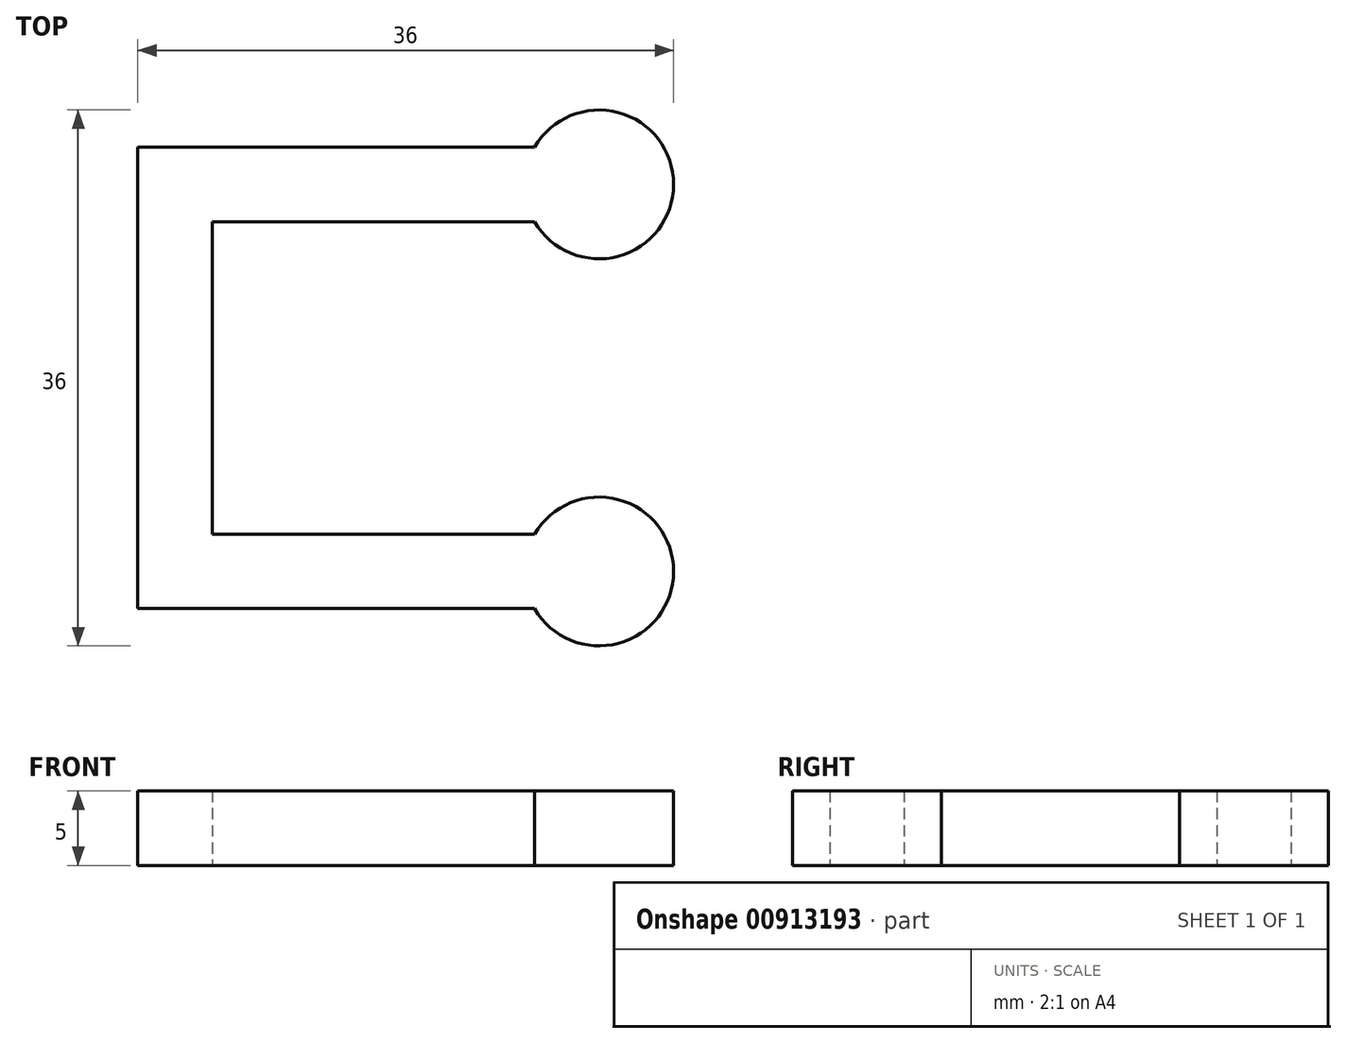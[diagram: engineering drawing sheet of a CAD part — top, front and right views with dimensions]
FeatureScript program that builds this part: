
annotation { "Feature Type Name" : "Feature", "Feature Type Description" : "" }
export const myFeature = defineFeature(function(context is Context, id is Id, definition is map)
    precondition{}
    {
        {
            assignVariable(context, id + "F0", {"name" : "HangerThickness", "anyValue" : 5});
        }
        {
            var Q0;
            Q0=qCreatedBy(makeId("Top.planeOp"),FACE);
            var sketch = newSketch(context, id + "F1", { "sketchPlane" : qUnion([Q0])});
            skLineSegment(sketch, "E0.bottom", {"start": v(10.5, 10.5) * mm, "end": v(-10.5, 10.5) * mm});
            skLineSegment(sketch, "E0.top", {"start": v(10.5, -10.5) * mm, "end": v(-10.5, -10.5) * mm});
            skLineSegment(sketch, "E0.left", {"start": v(10.5, 10.5) * mm, "end": v(10.5, -10.5) * mm});
            skLineSegment(sketch, "E0.right", {"start": v(-10.5, 10.5) * mm, "end": v(-10.5, -10.5) * mm});
            skPoint(sketch, "E0.middle", {"position": v(0, 0) * mm});
            skLineSegment(sketch, "E1.bottom", {"start": v(-15.5, 15.5) * mm, "end": v(15.5, 15.5) * mm});
            skLineSegment(sketch, "E1.top", {"start": v(-15.5, 10.5) * mm, "end": v(15.5, 10.5) * mm});
            skLineSegment(sketch, "E1.left", {"start": v(-15.5, 15.5) * mm, "end": v(-15.5, 10.5) * mm});
            skLineSegment(sketch, "E1.right", {"start": v(15.5, 15.5) * mm, "end": v(15.5, 10.5) * mm});
            skPoint(sketch, "E2", {"position": v(0, 10.5) * mm});
            skLineSegment(sketch, "E3.bottom", {"start": v(-10.5, 10.5) * mm, "end": v(-15.5, 10.5) * mm});
            skLineSegment(sketch, "E3.top", {"start": v(-10.5, -15.5) * mm, "end": v(-15.5, -15.5) * mm});
            skLineSegment(sketch, "E3.left", {"start": v(-10.5, 10.5) * mm, "end": v(-10.5, -15.5) * mm});
            skLineSegment(sketch, "E3.right", {"start": v(-15.5, 10.5) * mm, "end": v(-15.5, -15.5) * mm});
            skPoint(sketch, "E4", {"position": v(-13, -15.5) * mm});
            skPoint(sketch, "E5", {"position": v(15.5, 13) * mm});
            skCircle(sketch, "E6", {"center": v(15.5, 13) * mm, "radius": 5 * mm});
            skLineSegment(sketch, "E7.bottom", {"start": v(-10.5, -15.5) * mm, "end": v(15.5, -15.5) * mm});
            skLineSegment(sketch, "E7.top", {"start": v(-10.5, -10.5) * mm, "end": v(15.5, -10.5) * mm});
            skLineSegment(sketch, "E7.left", {"start": v(-10.5, -15.5) * mm, "end": v(-10.5, -10.5) * mm});
            skLineSegment(sketch, "E7.right", {"start": v(15.5, -15.5) * mm, "end": v(15.5, -10.5) * mm});
            skPoint(sketch, "E8", {"position": v(15.5, -13) * mm});
            skCircle(sketch, "E9", {"center": v(15.5, -13) * mm, "radius": 5 * mm});
            skSolve(sketch);
        }
        {
            var Q0;
            {var subQ0=sQuery(id+"F1.wireOp",EDGE,"E3.top");Q0=makeQuery(id+"F1.imprint","IMPRINT",FACE,{"disambiguationData":[TD([[makeQuery(id+"F1.imprint","IMPRINT",EDGE,{"derivedFrom":subQ0}),1.0]])]});}
            var Q1;
            {var subQ1=sQuery(id+"F1.wireOp",EDGE,"E0.right");Q1=makeQuery(id+"F1.imprint","IMPRINT",FACE,{"disambiguationData":[TD([[makeQuery(id+"F1.imprint","IMPRINT",EDGE,{"derivedFrom":subQ1}),-1.0]])]});}
            var Q2;
            {var subQ1=sQuery(id+"F1.wireOp",EDGE,"E0.right");Q2=makeQuery(id+"F1.imprint","IMPRINT",FACE,{"disambiguationData":[TD([[makeQuery(id+"F1.imprint","IMPRINT",EDGE,{"derivedFrom":subQ1}),-1.0]])]});}
            var Q3;
            {var subQ1=sQuery(id+"F1.wireOp",EDGE,"E0.bottom");Q3=makeQuery(id+"F1.imprint","IMPRINT",FACE,{"disambiguationData":[TD([[makeQuery(id+"F1.imprint","IMPRINT",EDGE,{"derivedFrom":subQ1}),-1.0]])]});}
            var Q4;
            {var subQ0=sQuery(id+"F1.wireOp",EDGE,"E1.right");Q4=makeQuery(id+"F1.imprint","IMPRINT",FACE,{"disambiguationData":[TD([[makeQuery(id+"F1.imprint","IMPRINT",EDGE,{"derivedFrom":subQ0}),-1.0]])]});}
            var Q5;
            {var subQ0=sQuery(id+"F1.wireOp",EDGE,"E1.right");Q5=makeQuery(id+"F1.imprint","IMPRINT",FACE,{"disambiguationData":[TD([[makeQuery(id+"F1.imprint","IMPRINT",EDGE,{"derivedFrom":subQ0}),1.0]])]});}
            var Q6;
            {var subQ1=sQuery(id+"F1.wireOp",EDGE,"E0.top");Q6=makeQuery(id+"F1.imprint","IMPRINT",FACE,{"disambiguationData":[TD([[makeQuery(id+"F1.imprint","IMPRINT",EDGE,{"derivedFrom":subQ1}),1.0]])]});}
            var Q7;
            {var subQ0=sQuery(id+"F1.wireOp",EDGE,"E7.right");Q7=makeQuery(id+"F1.imprint","IMPRINT",FACE,{"disambiguationData":[TD([[makeQuery(id+"F1.imprint","IMPRINT",EDGE,{"derivedFrom":subQ0}),1.0]])]});}
            var Q8;
            {var subQ0=sQuery(id+"F1.wireOp",EDGE,"E7.right");Q8=makeQuery(id+"F1.imprint","IMPRINT",FACE,{"disambiguationData":[TD([[makeQuery(id+"F1.imprint","IMPRINT",EDGE,{"derivedFrom":subQ0}),-1.0]])]});}
            extrude(context, id + "F2", {"entities" : qUnion([Q0, Q1, Q2, Q3, Q4, Q5, Q6, Q7, Q8]), "depth" : (getVariable(context, 'HangerThickness')) * mm, "offsetDistance" : 25 * mm});
        }
    });
